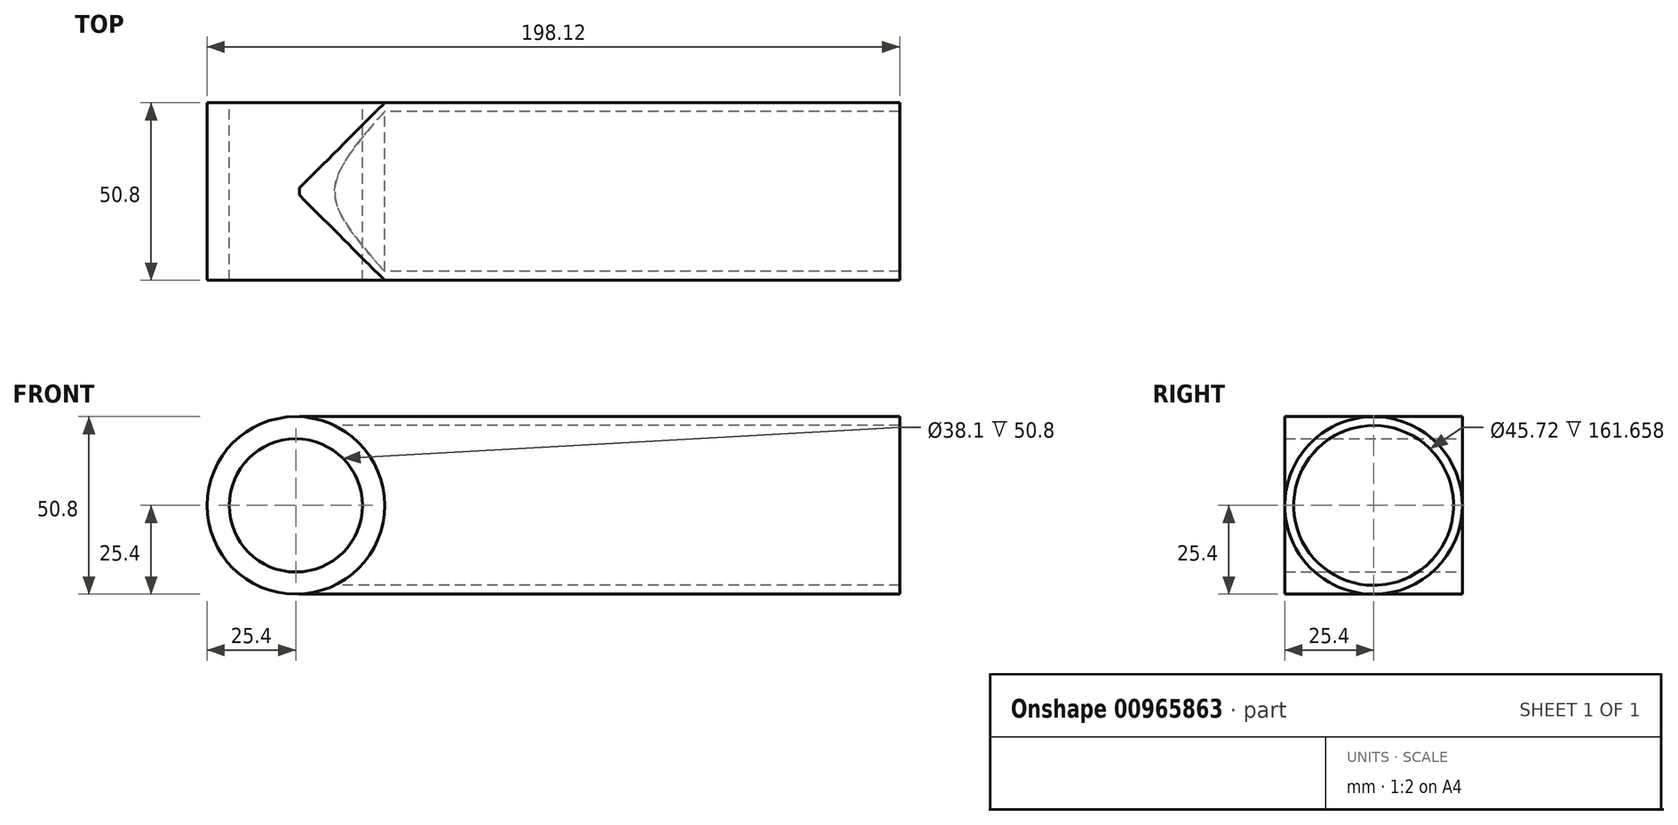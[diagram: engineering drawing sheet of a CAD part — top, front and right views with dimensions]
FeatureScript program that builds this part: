
annotation { "Feature Type Name" : "Feature", "Feature Type Description" : "" }
export const myFeature = defineFeature(function(context is Context, id is Id, definition is map)
    precondition{}
    {
        {
            var Q0;
            Q0=qCreatedBy(makeId("Front.planeOp"),FACE);
            var sketch = newSketch(context, id + "F0", { "sketchPlane" : qUnion([Q0])});
            skCircle(sketch, "E0", {"center": v(0, 0) * mm, "radius": 19.05 * mm});
            skCircle(sketch, "E1", {"center": v(0, 0) * mm, "radius": 25.4 * mm});
            skSolve(sketch);
        }
        {
            var Q0;
            Q0 = qSketchRegion(id + "F0", true);
            extrude(context, id + "F1", {"entities" : qUnion([Q0]), "depth" : 50.8 * mm, "offsetDistance" : 25.4 * mm});
        }
        {
            var Q0;
            Q0=qCreatedBy(makeId("Right.planeOp"),FACE);
            cPlane(context, id + "F2", {"entities" : qUnion([Q0]), "cplaneType" : CPlaneType.OFFSET, "offset" : 20.32 * mm, "width" : 152.4 * mm, "height" : 152.4 * mm});
        }
        {
            var Q0;
            Q0=qCreatedBy(id+"F2.planeOp",FACE);
            var sketch = newSketch(context, id + "F3", { "sketchPlane" : qUnion([Q0])});
            skLineSegment(sketch, "E2", {"start": v(0, 0) * mm, "end": v(-12.7, 0) * mm});
            skLineSegment(sketch, "E3", {"start": v(0, 0) * mm, "end": v(-25.4, 0) * mm});
            skCircle(sketch, "E4", {"center": v(-25.4, 0) * mm, "radius": 25.4 * mm});
            skCircle(sketch, "E5", {"center": v(-25.4, 0) * mm, "radius": 22.86 * mm});
            skSolve(sketch);
        }
        {
            var Q0;
            Q0 = qSketchRegion(id + "F3", true);
            extrude(context, id + "F4", {"entities" : qUnion([Q0]), "operationType" : NewBodyOperationType.ADD, "depth" : 152.4 * mm, "offsetDistance" : 25.4 * mm});
        }
        {
            var Q0;
            Q0 = qSketchRegion(id + "F3", true);
            extrude(context, id + "F5", {"entities" : qUnion([Q0]), "operationType" : NewBodyOperationType.ADD, "oppositeDirection" : true, "depth" : 19.3 * mm, "offsetDistance" : 25.4 * mm});
        }
        {
            var Q0;
            Q0=qCreatedBy(makeId("Front.planeOp"),FACE);
            var sketch = newSketch(context, id + "F6", { "sketchPlane" : qUnion([Q0])});
            skCircle(sketch, "E6", {"center": v(0, 0) * mm, "radius": 19.05 * mm});
            skSolve(sketch);
        }
        {
            var Q0;
            Q0 = qSketchRegion(id + "F6", true);
            extrude(context, id + "F7", {"entities" : qUnion([Q0]), "operationType" : NewBodyOperationType.REMOVE, "depth" : 64.77 * mm, "offsetDistance" : 25.4 * mm});
        }
    });
